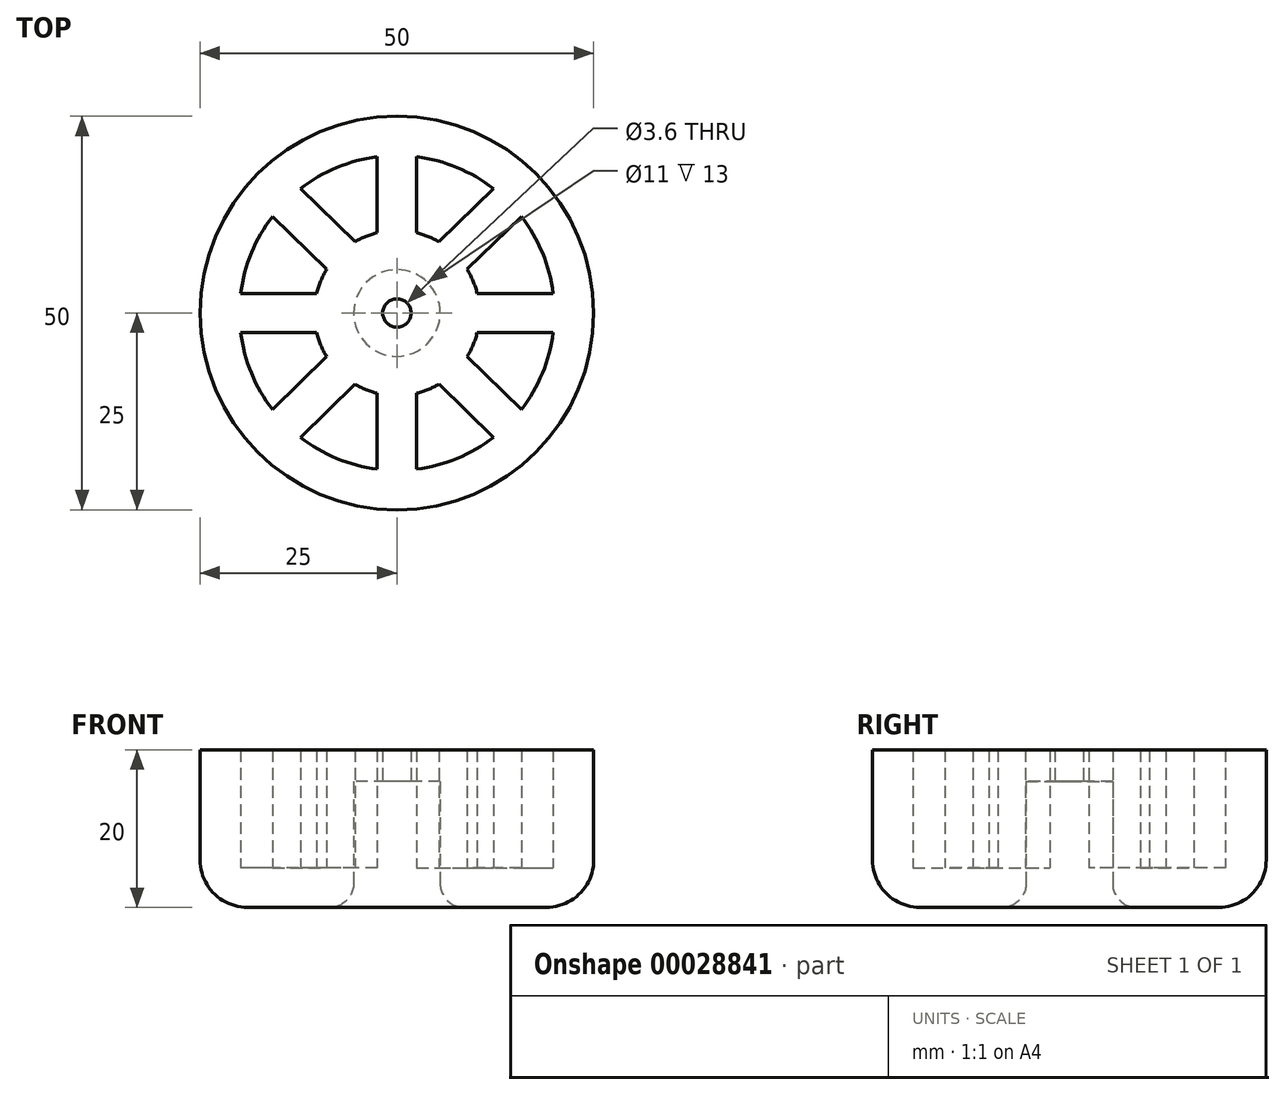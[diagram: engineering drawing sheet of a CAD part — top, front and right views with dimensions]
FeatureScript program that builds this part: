
annotation { "Feature Type Name" : "Feature", "Feature Type Description" : "" }
export const myFeature = defineFeature(function(context is Context, id is Id, definition is map)
    precondition{}
    {
        {
            var Q0;
            Q0=qCreatedBy(makeId("Top.planeOp"),FACE);
            var sketch = newSketch(context, id + "F0", { "sketchPlane" : qUnion([Q0])});
            skLineSegment(sketch, "E0", {"start": v(0, 0) * mm, "end": v(0, 20) * mm});
            skLineSegment(sketch, "E1", {"start": v(0, 0) * mm, "end": v(-20, 0) * mm});
            skLineSegment(sketch, "E2", {"start": v(-2.5, 19.84) * mm, "end": v(-2.5, 2.5) * mm});
            skLineSegment(sketch, "E3", {"start": v(-2.5, 2.5) * mm, "end": v(-19.84, 2.5) * mm});
            skArc(sketch, "E4", {"start": v(0, 25) * mm, "mid": v(-17.68, 17.68) * mm, "end": v(-25, 0) * mm});
            skArc(sketch, "E5", {"start": v(0, 20) * mm, "mid": v(-14.14, 14.14) * mm, "end": v(-20, 0) * mm});
            skLineSegment(sketch, "E6", {"start": v(0, 20) * mm, "end": v(0, 25) * mm});
            skLineSegment(sketch, "E7", {"start": v(-25, 0) * mm, "end": v(-20, 0) * mm});
            skArc(sketch, "E8", {"start": v(0, 5.5) * mm, "mid": v(-3.89, 3.89) * mm, "end": v(-5.5, 0) * mm});
            skArc(sketch, "E9", {"start": v(0, 1.8) * mm, "mid": v(-1.27, 1.27) * mm, "end": v(-1.8, 0) * mm});
            skArc(sketch, "E10", {"start": v(0, 10.5) * mm, "mid": v(-7.42, 7.42) * mm, "end": v(-10.5, 0) * mm});
            skLineSegment(sketch, "E11", {"start": v(-15.8, 12.26) * mm, "end": v(-8.91, 5.55) * mm});
            skLineSegment(sketch, "E12", {"start": v(-5.33, 9.04) * mm, "end": v(-12.26, 15.8) * mm});
            skLineSegment(sketch, "E13", {"start": v(-2.5, 10.2) * mm, "end": v(-5.33, 9.04) * mm, "construction": true});
            skLineSegment(sketch, "E14", {"start": v(-8.91, 5.55) * mm, "end": v(-10.2, 2.5) * mm, "construction": true});
            skLineSegment(sketch, "E15", {"start": v(-19.84, 2.5) * mm, "end": v(-15.8, 12.26) * mm, "construction": true});
            skLineSegment(sketch, "E16", {"start": v(-12.26, 15.8) * mm, "end": v(-2.5, 19.84) * mm, "construction": true});
            skSolve(sketch);
        }
        {
            var Q0;
            {var subQ1=sQuery(id+"F0.wireOp",EDGE,"E3");var subQ5=sQuery(id+"F0.wireOp",EDGE,"E5");var subQ6=makeQuery(id+"F0.imprint","INTERSECT",VERTEX,{"derivedFrom":[subQ1,subQ5]});Q0=makeQuery(id+"F0.imprint","IMPRINT",FACE,{"disambiguationData":[TD([[makeQuery(id+"F0.imprint","IMPRINT",EDGE,{"disambiguationData":[TD([[subQ6,1.0]])],"derivedFrom":subQ1}),1.0]])]});}
            var Q1;
            {var subQ0=sQuery(id+"F0.wireOp",EDGE,"E10");var subQ5=sQuery(id+"F0.wireOp",EDGE,"E2");var subQ6=makeQuery(id+"F0.imprint","INTERSECT",VERTEX,{"derivedFrom":[subQ5,subQ0]});Q1=makeQuery(id+"F0.imprint","IMPRINT",FACE,{"disambiguationData":[TD([[makeQuery(id+"F0.imprint","IMPRINT",EDGE,{"disambiguationData":[TD([[subQ6,-1.0]])],"derivedFrom":subQ5}),-1.0]])]});}
            var Q2;
            {var subQ3=sQuery(id+"F0.wireOp",EDGE,"E1");var subQ5=sQuery(id+"F0.wireOp",EDGE,"E8");var subQ7=makeQuery(id+"F0.imprint","INTERSECT",VERTEX,{"derivedFrom":[subQ3,subQ5]});Q2=makeQuery(id+"F0.imprint","IMPRINT",FACE,{"disambiguationData":[TD([[makeQuery(id+"F0.imprint","IMPRINT",EDGE,{"disambiguationData":[TD([[subQ7,-1.0]])],"derivedFrom":subQ3}),-1.0]])]});}
            var Q3;
            {var subQ0=sQuery(id+"F0.wireOp",EDGE,"E9");Q3=makeQuery(id+"F0.imprint","IMPRINT",FACE,{"disambiguationData":[TD([[makeQuery(id+"F0.imprint","IMPRINT",EDGE,{"derivedFrom":subQ0}),-1.0]])]});}
            var Q4;
            {var subQ1=sQuery(id+"F0.wireOp",EDGE,"E2");var subQ5=sQuery(id+"F0.wireOp",EDGE,"E5");var subQ6=makeQuery(id+"F0.imprint","INTERSECT",VERTEX,{"derivedFrom":[subQ1,subQ5]});Q4=makeQuery(id+"F0.imprint","IMPRINT",FACE,{"disambiguationData":[TD([[makeQuery(id+"F0.imprint","IMPRINT",EDGE,{"disambiguationData":[TD([[subQ6,-1.0]])],"derivedFrom":subQ1}),1.0]])]});}
            var Q5;
            {var subQ1=sQuery(id+"F0.wireOp",EDGE,"E11");Q5=makeQuery(id+"F0.imprint","IMPRINT",FACE,{"disambiguationData":[TD([[makeQuery(id+"F0.imprint","IMPRINT",EDGE,{"derivedFrom":subQ1}),1.0]])]});}
            var Q6;
            {var subQ3=sQuery(id+"F0.wireOp",EDGE,"E0");var subQ5=sQuery(id+"F0.wireOp",EDGE,"E8");var subQ7=makeQuery(id+"F0.imprint","INTERSECT",VERTEX,{"derivedFrom":[subQ3,subQ5]});Q6=makeQuery(id+"F0.imprint","IMPRINT",FACE,{"disambiguationData":[TD([[makeQuery(id+"F0.imprint","IMPRINT",EDGE,{"disambiguationData":[TD([[subQ7,-1.0]])],"derivedFrom":subQ3}),1.0]])]});}
            var Q7;
            Q7=makeQuery(id+"F0.imprint","IMPRINT",FACE,{"disambiguationData":[TD([[makeQuery(id+"F0.imprint","IMPRINT",EDGE,{"derivedFrom":sQuery(id+"F0.wireOp",EDGE,"E4")}),1.0]])]});
            var Q8;
            {var subQ1=sQuery(id+"F0.wireOp",EDGE,"E3");var subQ3=sQuery(id+"F0.wireOp",EDGE,"E2");var subQ5=makeQuery(id+"F0.imprint","INTERSECT",VERTEX,{"derivedFrom":[subQ3,subQ1]});Q8=makeQuery(id+"F0.imprint","IMPRINT",FACE,{"disambiguationData":[TD([[makeQuery(id+"F0.imprint","IMPRINT",EDGE,{"disambiguationData":[TD([[subQ5,1.0]])],"derivedFrom":subQ3}),-1.0]])]});}
            extrude(context, id + "F1", {"entities" : qUnion([Q0, Q1, Q2, Q3, Q4, Q5, Q6, Q7, Q8]), "depth" : 15 * mm});
        }
        {
            var Q0;
            {var subQ0=sQuery(id+"F0.wireOp",EDGE,"E9");Q0=makeQuery(id+"F0.imprint","IMPRINT",FACE,{"disambiguationData":[TD([[makeQuery(id+"F0.imprint","IMPRINT",EDGE,{"derivedFrom":subQ0}),-1.0]])]});}
            var Q1;
            {var subQ1=sQuery(id+"F0.wireOp",EDGE,"E3");var subQ3=sQuery(id+"F0.wireOp",EDGE,"E2");var subQ5=makeQuery(id+"F0.imprint","INTERSECT",VERTEX,{"derivedFrom":[subQ3,subQ1]});Q1=makeQuery(id+"F0.imprint","IMPRINT",FACE,{"disambiguationData":[TD([[makeQuery(id+"F0.imprint","IMPRINT",EDGE,{"disambiguationData":[TD([[subQ5,1.0]])],"derivedFrom":subQ3}),-1.0]])]});}
            extrude(context, id + "F2", {"entities" : qUnion([Q0, Q1]), "operationType" : NewBodyOperationType.REMOVE, "depth" : 11 * mm});
        }
        {
            var Q0;
            {var subQ1=sQuery(id+"F0.wireOp",EDGE,"E3");var subQ5=sQuery(id+"F0.wireOp",EDGE,"E5");var subQ6=makeQuery(id+"F0.imprint","INTERSECT",VERTEX,{"derivedFrom":[subQ1,subQ5]});Q0=makeQuery(id+"F0.imprint","IMPRINT",FACE,{"disambiguationData":[TD([[makeQuery(id+"F0.imprint","IMPRINT",EDGE,{"disambiguationData":[TD([[subQ6,1.0]])],"derivedFrom":subQ1}),1.0]])]});}
            var Q1;
            {var subQ0=sQuery(id+"F0.wireOp",EDGE,"E10");var subQ5=sQuery(id+"F0.wireOp",EDGE,"E2");var subQ6=makeQuery(id+"F0.imprint","INTERSECT",VERTEX,{"derivedFrom":[subQ5,subQ0]});Q1=makeQuery(id+"F0.imprint","IMPRINT",FACE,{"disambiguationData":[TD([[makeQuery(id+"F0.imprint","IMPRINT",EDGE,{"disambiguationData":[TD([[subQ6,-1.0]])],"derivedFrom":subQ5}),-1.0]])]});}
            var Q2;
            {var subQ3=sQuery(id+"F0.wireOp",EDGE,"E1");var subQ5=sQuery(id+"F0.wireOp",EDGE,"E8");var subQ7=makeQuery(id+"F0.imprint","INTERSECT",VERTEX,{"derivedFrom":[subQ3,subQ5]});Q2=makeQuery(id+"F0.imprint","IMPRINT",FACE,{"disambiguationData":[TD([[makeQuery(id+"F0.imprint","IMPRINT",EDGE,{"disambiguationData":[TD([[subQ7,-1.0]])],"derivedFrom":subQ3}),-1.0]])]});}
            var Q3;
            {var subQ0=sQuery(id+"F0.wireOp",EDGE,"E11");Q3=makeQuery(id+"F0.imprint","IMPRINT",FACE,{"disambiguationData":[TD([[makeQuery(id+"F0.imprint","IMPRINT",EDGE,{"derivedFrom":subQ0}),-1.0]])]});}
            var Q4;
            {var subQ1=sQuery(id+"F0.wireOp",EDGE,"E2");var subQ5=sQuery(id+"F0.wireOp",EDGE,"E5");var subQ6=makeQuery(id+"F0.imprint","INTERSECT",VERTEX,{"derivedFrom":[subQ1,subQ5]});Q4=makeQuery(id+"F0.imprint","IMPRINT",FACE,{"disambiguationData":[TD([[makeQuery(id+"F0.imprint","IMPRINT",EDGE,{"disambiguationData":[TD([[subQ6,-1.0]])],"derivedFrom":subQ1}),1.0]])]});}
            var Q5;
            {var subQ0=sQuery(id+"F0.wireOp",EDGE,"E12");Q5=makeQuery(id+"F0.imprint","IMPRINT",FACE,{"disambiguationData":[TD([[makeQuery(id+"F0.imprint","IMPRINT",EDGE,{"derivedFrom":subQ0}),-1.0]])]});}
            var Q6;
            {var subQ1=sQuery(id+"F0.wireOp",EDGE,"E11");Q6=makeQuery(id+"F0.imprint","IMPRINT",FACE,{"disambiguationData":[TD([[makeQuery(id+"F0.imprint","IMPRINT",EDGE,{"derivedFrom":subQ1}),1.0]])]});}
            var Q7;
            {var subQ3=sQuery(id+"F0.wireOp",EDGE,"E0");var subQ5=sQuery(id+"F0.wireOp",EDGE,"E8");var subQ7=makeQuery(id+"F0.imprint","INTERSECT",VERTEX,{"derivedFrom":[subQ3,subQ5]});Q7=makeQuery(id+"F0.imprint","IMPRINT",FACE,{"disambiguationData":[TD([[makeQuery(id+"F0.imprint","IMPRINT",EDGE,{"disambiguationData":[TD([[subQ7,-1.0]])],"derivedFrom":subQ3}),1.0]])]});}
            var Q8;
            Q8=makeQuery(id+"F0.imprint","IMPRINT",FACE,{"disambiguationData":[TD([[makeQuery(id+"F0.imprint","IMPRINT",EDGE,{"derivedFrom":sQuery(id+"F0.wireOp",EDGE,"E4")}),1.0]])]});
            extrude(context, id + "F3", {"entities" : qUnion([Q0, Q1, Q2, Q3, Q4, Q5, Q6, Q7, Q8]), "oppositeDirection" : true, "depth" : 5 * mm});
        }
        {
            var Q0;
            Q0=makeQuery(id+"F1.opExtrude","SWEPT_BODY",BODY,{"disambiguationData":[OSD([sQuery(id+"F0.wireOp",EDGE,"E0"),sQuery(id+"F0.wireOp",EDGE,"E1"),sQuery(id+"F0.wireOp",EDGE,"E2"),sQuery(id+"F0.wireOp",EDGE,"E3"),sQuery(id+"F0.wireOp",EDGE,"E4"),sQuery(id+"F0.wireOp",EDGE,"E5"),sQuery(id+"F0.wireOp",EDGE,"E6"),sQuery(id+"F0.wireOp",EDGE,"E7"),sQuery(id+"F0.wireOp",EDGE,"E9"),sQuery(id+"F0.wireOp",EDGE,"E10"),sQuery(id+"F0.wireOp",EDGE,"E11"),sQuery(id+"F0.wireOp",EDGE,"E12")])]});
            var Q1;
            Q1=makeQuery(id+"F3.opExtrude","SWEPT_BODY",BODY,{"disambiguationData":[OSD([sQuery(id+"F0.wireOp",EDGE,"E0"),sQuery(id+"F0.wireOp",EDGE,"E1"),sQuery(id+"F0.wireOp",EDGE,"E4"),sQuery(id+"F0.wireOp",EDGE,"E6"),sQuery(id+"F0.wireOp",EDGE,"E7"),sQuery(id+"F0.wireOp",EDGE,"E8")])]});
            booleanBodies(context, id + "F4", {"operationType" : BooleanOperationType.UNION, "tools" : qUnion([Q0, Q1])});
        }
        {
            var Q0;
            Q0=makeQuery(id+"F3.opExtrude","CAP_EDGE",EDGE,{"disambiguationData":[OSD([sQuery(id+"F0.wireOp",EDGE,"E4")])],"isStart":false});
            fillet(context, id + "F5", {"entities" : qUnion([Q0]), "radius" : 6 * mm, "tangentPropagation" : true, "allowEdgeOverflow" : false});
        }
        {
            var Q0;
            Q0=makeQuery(id+"F3.opExtrude","CAP_EDGE",EDGE,{"disambiguationData":[OSD([sQuery(id+"F0.wireOp",EDGE,"E8")])],"isStart":false});
            fillet(context, id + "F6", {"entities" : qUnion([Q0]), "radius" : 3 * mm, "tangentPropagation" : true, "allowEdgeOverflow" : false});
        }
        {
            var Q0;
            Q0=makeQuery(id+"F1.opExtrude","SWEPT_BODY",BODY,{"disambiguationData":[OSD([sQuery(id+"F0.wireOp",EDGE,"E0"),sQuery(id+"F0.wireOp",EDGE,"E1"),sQuery(id+"F0.wireOp",EDGE,"E2"),sQuery(id+"F0.wireOp",EDGE,"E3"),sQuery(id+"F0.wireOp",EDGE,"E4"),sQuery(id+"F0.wireOp",EDGE,"E5"),sQuery(id+"F0.wireOp",EDGE,"E6"),sQuery(id+"F0.wireOp",EDGE,"E7"),sQuery(id+"F0.wireOp",EDGE,"E9"),sQuery(id+"F0.wireOp",EDGE,"E10"),sQuery(id+"F0.wireOp",EDGE,"E11"),sQuery(id+"F0.wireOp",EDGE,"E12")])]});
            var Q1;
            {var subQ0=sQuery(id+"F0.wireOp",EDGE,"E1");var subQ1=sQuery(id+"F0.wireOp",EDGE,"E7");Q1=makeQuery(id+"F4.opBoolean","MERGE",FACE,{"derivedFrom":[makeQuery(id+"F1.opExtrude","SWEPT_FACE",FACE,{"disambiguationData":[OSD([subQ0,subQ1])]}),makeQuery(id+"F3.opExtrude","SWEPT_FACE",FACE,{"disambiguationData":[OSD([subQ0,subQ1])]})]});}
            mirror(context, id + "F7", {"operationType" : NewBodyOperationType.ADD, "entities" : qUnion([Q0]), "mirrorPlane" : qUnion([Q1])});
        }
        {
            var Q0;
            Q0=makeQuery(id+"F1.opExtrude","SWEPT_BODY",BODY,{"disambiguationData":[OSD([sQuery(id+"F0.wireOp",EDGE,"E0"),sQuery(id+"F0.wireOp",EDGE,"E1"),sQuery(id+"F0.wireOp",EDGE,"E2"),sQuery(id+"F0.wireOp",EDGE,"E3"),sQuery(id+"F0.wireOp",EDGE,"E4"),sQuery(id+"F0.wireOp",EDGE,"E5"),sQuery(id+"F0.wireOp",EDGE,"E6"),sQuery(id+"F0.wireOp",EDGE,"E7"),sQuery(id+"F0.wireOp",EDGE,"E9"),sQuery(id+"F0.wireOp",EDGE,"E10"),sQuery(id+"F0.wireOp",EDGE,"E11"),sQuery(id+"F0.wireOp",EDGE,"E12")])]});
            var Q1;
            {var subQ0=sQuery(id+"F0.wireOp",EDGE,"E0");var subQ1=sQuery(id+"F0.wireOp",EDGE,"E6");Q1=makeQuery(id+"F7.opPattern","COPY",FACE,{"derivedFrom":makeQuery(id+"F4.opBoolean","MERGE",FACE,{"derivedFrom":[makeQuery(id+"F1.opExtrude","SWEPT_FACE",FACE,{"disambiguationData":[OSD([subQ0,subQ1])]}),makeQuery(id+"F3.opExtrude","SWEPT_FACE",FACE,{"disambiguationData":[OSD([subQ0,subQ1])]})]}),"instanceName":"1"});}
            mirror(context, id + "F8", {"operationType" : NewBodyOperationType.ADD, "entities" : qUnion([Q0]), "mirrorPlane" : qUnion([Q1])});
        }
    });
